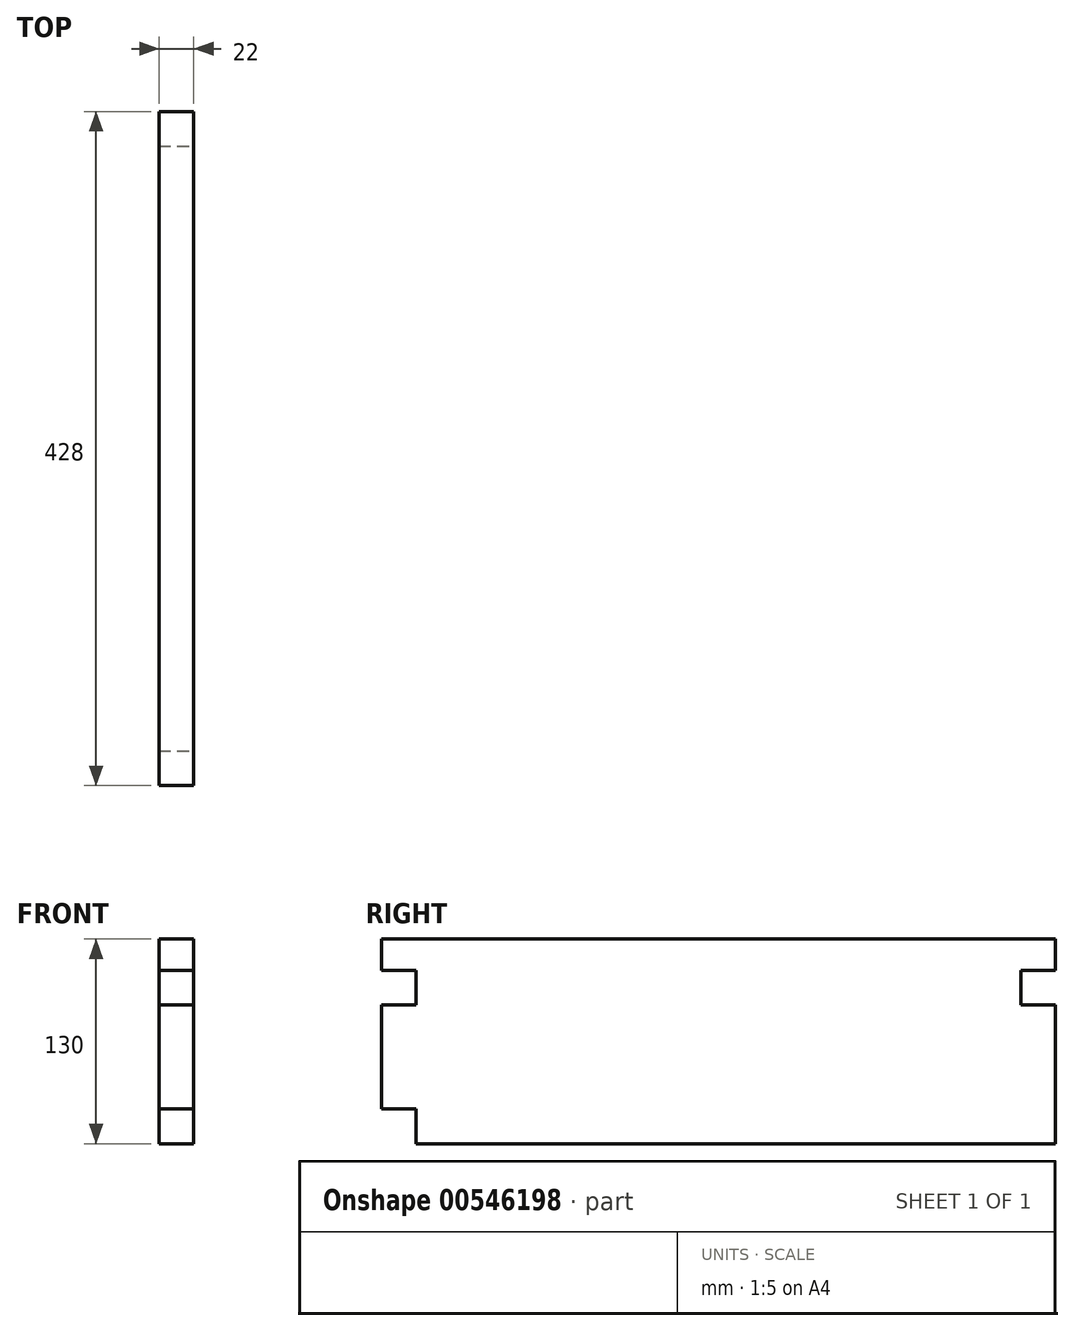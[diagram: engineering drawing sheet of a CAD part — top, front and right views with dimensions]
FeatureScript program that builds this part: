
annotation { "Feature Type Name" : "Feature", "Feature Type Description" : "" }
export const myFeature = defineFeature(function(context is Context, id is Id, definition is map)
    precondition{}
    {
        {
            var Q0;
            Q0=qCreatedBy(makeId("Right.planeOp"),FACE);
            var sketch = newSketch(context, id + "F0", { "sketchPlane" : qUnion([Q0])});
            skLineSegment(sketch, "E0.bottom", {"start": v(0, 0) * mm, "end": v(428, 0) * mm});
            skLineSegment(sketch, "E0.top", {"start": v(0, 130) * mm, "end": v(428, 130) * mm});
            skLineSegment(sketch, "E0.left", {"start": v(0, 0) * mm, "end": v(0, 130) * mm});
            skLineSegment(sketch, "E0.right", {"start": v(428, 0) * mm, "end": v(428, 130) * mm});
            skSolve(sketch);
        }
        {
            var Q0;
            Q0=makeQuery(id+"F0.imprint","IMPRINT",FACE,{"disambiguationData":[TD([[makeQuery(id+"F0.imprint","IMPRINT",EDGE,{"derivedFrom":sQuery(id+"F0.wireOp",EDGE,"E0.bottom")}),1.0]])]});
            extrude(context, id + "F1", {"entities" : qUnion([Q0]), "depth" : 22 * mm, "offsetDistance" : 25 * mm});
        }
        {
            var Q0;
            Q0=makeQuery(id+"F1.opExtrude","CAP_FACE",FACE,{"disambiguationData":[OSD([sQuery(id+"F0.wireOp",EDGE,"E0.bottom"),sQuery(id+"F0.wireOp",EDGE,"E0.top"),sQuery(id+"F0.wireOp",EDGE,"E0.left"),sQuery(id+"F0.wireOp",EDGE,"E0.right")])],"isStart":false});
            var sketch = newSketch(context, id + "F2", { "sketchPlane" : qUnion([Q0])});
            skLineSegment(sketch, "E1", {"start": v(214, 130) * mm, "end": v(214, 0) * mm});
            skLineSegment(sketch, "E2.bottom", {"start": v(0, 0) * mm, "end": v(22, 0) * mm});
            skLineSegment(sketch, "E2.top", {"start": v(0, 22) * mm, "end": v(22, 22) * mm});
            skLineSegment(sketch, "E2.left", {"start": v(0, 0) * mm, "end": v(0, 22) * mm});
            skLineSegment(sketch, "E2.right", {"start": v(22, 0) * mm, "end": v(22, 22) * mm});
            skLineSegment(sketch, "E3.bottom", {"start": v(22, 22) * mm, "end": v(0, 22) * mm});
            skLineSegment(sketch, "E3.top", {"start": v(22, 44) * mm, "end": v(0, 44) * mm});
            skLineSegment(sketch, "E3.left", {"start": v(22, 22) * mm, "end": v(22, 44) * mm});
            skLineSegment(sketch, "E3.right", {"start": v(0, 22) * mm, "end": v(0, 44) * mm});
            skLineSegment(sketch, "E4.bottom", {"start": v(0, 44) * mm, "end": v(22, 44) * mm});
            skLineSegment(sketch, "E4.top", {"start": v(0, 66) * mm, "end": v(22, 66) * mm});
            skLineSegment(sketch, "E4.left", {"start": v(0, 44) * mm, "end": v(0, 66) * mm});
            skLineSegment(sketch, "E4.right", {"start": v(22, 44) * mm, "end": v(22, 66) * mm});
            skLineSegment(sketch, "E5.top", {"start": v(0, 88) * mm, "end": v(22, 88) * mm});
            skLineSegment(sketch, "E5.left", {"start": v(0, 66) * mm, "end": v(0, 88) * mm});
            skLineSegment(sketch, "E5.right", {"start": v(22, 66) * mm, "end": v(22, 88) * mm});
            skLineSegment(sketch, "E6.top", {"start": v(0, 110) * mm, "end": v(22, 110) * mm});
            skLineSegment(sketch, "E6.left", {"start": v(0, 88) * mm, "end": v(0, 110) * mm});
            skLineSegment(sketch, "E6.right", {"start": v(22, 88) * mm, "end": v(22, 110) * mm});
            skLineSegment(sketch, "E7.MirrorCS", {"start": v(428, 22) * mm, "end": v(406, 22) * mm});
            skLineSegment(sketch, "E8.MirrorCS", {"start": v(428, 44) * mm, "end": v(406, 44) * mm});
            skLineSegment(sketch, "E9.MirrorCS", {"start": v(406, 44) * mm, "end": v(428, 44) * mm});
            skLineSegment(sketch, "E10.MirrorCS", {"start": v(406, 22) * mm, "end": v(428, 22) * mm});
            skLineSegment(sketch, "E11.MirrorCS", {"start": v(428, 66) * mm, "end": v(406, 66) * mm});
            skLineSegment(sketch, "E12.MirrorCS", {"start": v(428, 88) * mm, "end": v(406, 88) * mm});
            skLineSegment(sketch, "E13.MirrorCS", {"start": v(428, 44) * mm, "end": v(428, 66) * mm});
            skLineSegment(sketch, "E14.MirrorCS", {"start": v(406, 0) * mm, "end": v(406, 22) * mm});
            skLineSegment(sketch, "E15.MirrorCS", {"start": v(428, 0) * mm, "end": v(428, 22) * mm});
            skLineSegment(sketch, "E16.MirrorCS", {"start": v(428, 0) * mm, "end": v(406, 0) * mm});
            skLineSegment(sketch, "E17.MirrorCS", {"start": v(406, 22) * mm, "end": v(406, 44) * mm});
            skLineSegment(sketch, "E18.MirrorCS", {"start": v(428, 22) * mm, "end": v(428, 44) * mm});
            skLineSegment(sketch, "E19.MirrorCS", {"start": v(428, 66) * mm, "end": v(428, 88) * mm});
            skLineSegment(sketch, "E20.MirrorCS", {"start": v(428, 88) * mm, "end": v(428, 110) * mm});
            skLineSegment(sketch, "E21.MirrorCS", {"start": v(406, 66) * mm, "end": v(406, 88) * mm});
            skLineSegment(sketch, "E22.MirrorCS", {"start": v(428, 110) * mm, "end": v(406, 110) * mm});
            skLineSegment(sketch, "E23.MirrorCS", {"start": v(406, 44) * mm, "end": v(406, 66) * mm});
            skLineSegment(sketch, "E24.MirrorCS", {"start": v(406, 88) * mm, "end": v(406, 110) * mm});
            skSolve(sketch);
        }
        {
            var Q0;
            Q0=makeQuery(id+"F2.imprint","IMPRINT",FACE,{"disambiguationData":[TD([[makeQuery(id+"F2.imprint","IMPRINT",EDGE,{"derivedFrom":sQuery(id+"F2.wireOp",EDGE,"E5.top")}),1.0]])]});
            var Q1;
            Q1=makeQuery(id+"F2.imprint","IMPRINT",FACE,{"disambiguationData":[TD([[makeQuery(id+"F2.imprint","IMPRINT",EDGE,{"derivedFrom":sQuery(id+"F2.wireOp",EDGE,"E4.bottom")}),1.0]])]});
            var Q2;
            Q2=makeQuery(id+"F2.imprint","IMPRINT",FACE,{"disambiguationData":[TD([[makeQuery(id+"F2.imprint","IMPRINT",EDGE,{"derivedFrom":sQuery(id+"F2.wireOp",EDGE,"E2.bottom")}),1.0]])]});
            var Q3;
            Q3=makeQuery(id+"F2.imprint","IMPRINT",FACE,{"disambiguationData":[TD([[makeQuery(id+"F2.imprint","IMPRINT",EDGE,{"derivedFrom":sQuery(id+"F2.wireOp",EDGE,"E10.MirrorCS")}),-1.0]])]});
            var Q4;
            Q4=makeQuery(id+"F2.imprint","IMPRINT",FACE,{"disambiguationData":[TD([[makeQuery(id+"F2.imprint","IMPRINT",EDGE,{"derivedFrom":sQuery(id+"F2.wireOp",EDGE,"E9.MirrorCS")}),1.0]])]});
            var Q5;
            Q5=makeQuery(id+"F2.imprint","IMPRINT",FACE,{"disambiguationData":[TD([[makeQuery(id+"F2.imprint","IMPRINT",EDGE,{"derivedFrom":sQuery(id+"F2.wireOp",EDGE,"E12.MirrorCS")}),-1.0]])]});
            extrude(context, id + "F3", {"entities" : qUnion([Q0, Q1, Q2, Q3, Q4, Q5]), "operationType" : NewBodyOperationType.REMOVE, "oppositeDirection" : true, "depth" : 25 * mm, "offsetDistance" : 25 * mm});
        }
    });
